# Revit family: Seating-Casual-Naughtone-Cloud_Plain_1.5_Seat
name_source: partatom
category: Furniture
revit_build: Autodesk Revit 2014 (Build: 20140709_2115(x64)
units: mm (PartAtom-declared; Revit-internal decimal feet)

## types (2) — shared parameters
Additional Materials = Additional material and finish options available. Please contact Naughtone direct for further information.
COBie Description = Designed by Naughtone, Cloud plain seating system's tactile, pillowy surround is designed to invite and comfort without consuming masses of space. Whether you are looking for somewhere to shelter or meet or simply to relax, cloud has a magnetic appeal.
Current Revision = 1
Depth = 750 mm
Length = 1100 mm
Manufacturer = Naughtone
Name = Furniture-Seating-Casual-Cloud_Plain
Product URL = http://www.naughtone.com
URL = http://www.naughtone.com
Uniclass = Pr_40_50_12_48
WarrantyDuration = 60
zero-valued in all types: Barcode, Cost, SerialNumber, TagNumber

## per-type parameters (varying)
| type | Description | Height | High Chair | Low Chair | Model | TypeName |
| CLO-P-1.5-HI | Cloud 1.5 Sofa with High Back | 1300 mm | Yes | No | Cloud 1.5 Sofa with High Back | 1100mmx750mm1300mm, Cloud Plain |
| CLO-P-1.5-LO | Cloud 1.5 Sofa with Low Back | 650 mm  [stored 2.13255 ft] | No | Yes | Cloud 1.5 Sofa with Low Back | 1100mmx750mm650mm, Cloud Plain Seating |

note: column(s) folded — value = type name in every type: AssetIdentifier, Product Code

note: [stored X ft] marks values corroborated as IEEE doubles in the binary element streams (Revit-internal decimal feet)

## geometry (parser evidence)
native form markers: Blend x2, Sweep x7
no freeform markers — native parametric forms only
